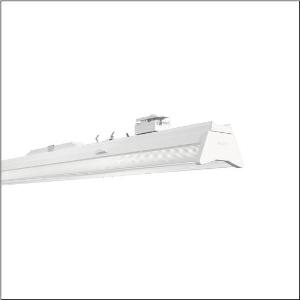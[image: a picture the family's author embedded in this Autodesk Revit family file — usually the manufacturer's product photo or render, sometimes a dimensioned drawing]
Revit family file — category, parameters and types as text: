
# Revit family: licross_r__11_performance_ho_51td16dn6exm_746f
name_source: partatom
category: Lighting Fixtures
units: mm (PartAtom-declared; Revit-internal decimal feet)

## family parameters
Cut with Voids When Loaded = No
Host = Face
Light Source = No
Part Type = Normal
Room Calculation Point = No
Round Connector Dimension = Use Diameter
Shared = No

## types (1)
- --- (1 x LED, 14180 lm, 81.4 W, 6500K)
    Apparent Load = 81 VA
    CIE Flux Codes = 63 87 95 78 100
    Color Rendering = 80
    Color Temperature = 6500K
    Default Elevation = 1800 mm
    Description = Licross® 11 Performance HO, luminaire insert, of sheet steel, galvanised, coil coated, white, length: 1.500mm, width: 120mm, height: 123mm, LED rated luminous flux: 14.180lm, light colour: 865, control gear: DALI 2, with plug, 5-pole, with phase selection, mains connection: 220..240V, AC, 50/60Hz, rated input power: 81W, halogen-free wiring, primary light control with lens, of plastic, primary optical cover: cover, of PMMA, light emission: direct/indirect distribution, primary light characteristic: symmetric, protection rating (complete): IP54, insulation class (complete): insulation class I (protective earthing), certification: CE, ENEC, VDE, UKCA, protection symbol: D if used in an environment with non-conductive dust loads with corresponding accessories, impact resistance: IK06, permissible ambient temperature for indoor applications: -25..+35°C, corresponds to IFS (International Featured Standards) requirements for safety and quality in the food industry, reducing of maximum allowable ambient temperature of 5°C with ceiling mounting, LABS conformity tested according to VDMA 24364:2018-05, packaging unit: 1 piece
    Height = 114 mm
    Lamp = 1 x LED
    Lamp Light Flux = 14180 lm
    Lamp Power = 81.4 W
    Lamp count = 1
    Length = 1500 mm
    Luminous efficacy = 174 lm/W
    Manufacturer = Siteco
    ModVariant = No
    Model = 51TD16DN6EXM
    Mounting Place = Ceiling
    Mounting Type = Pendant
    Number of Poles = 1
    OnlyDefault = Yes
    Power Factor = 1
    Product Name = Licross® 11 Performance HO
    Product group = luminaire insert
    ProductGroupID = 901
    Protection Class = Protection class I
    Protection Degree = IP 54
    RLX_Detail_Level = 1
    RLX_Emergency_Light_Flux = 0 lm
    RLX_Emergency_Type = 0
    RLX_Emergency_Type_DB = No
    RlxData = <blob elided: 34149 chars, md5=66e3ef7d>
    Socket = socket
    Standby Power = 0 W
    System Light Flux = 14180 lm
    System Power = 81 W
    Type Comments = factory setting: luminous flux: 100 % | dim-lin: 254 | 550 mA
    Type Image = l_1256138.jpg
    URL = http://relux.com
    VarID = @adj_026867
    Voltage = 0 V
    Weight = 0.00 kg
    Width = 120 mm

## geometry (parser evidence)
native form markers: Blend x4, Sweep x13
no freeform markers — native parametric forms only
